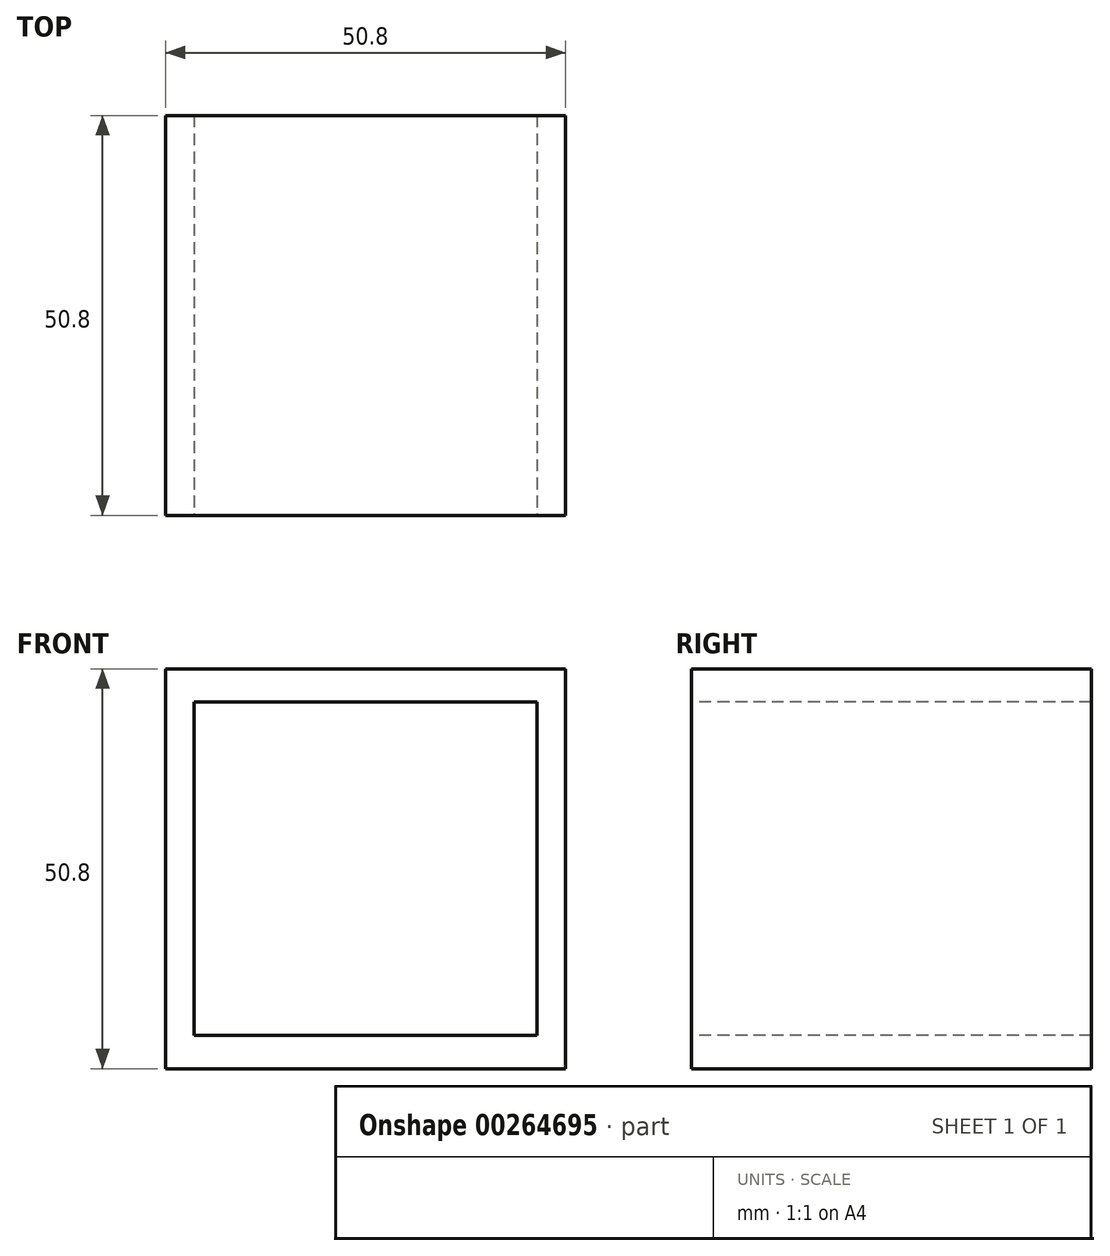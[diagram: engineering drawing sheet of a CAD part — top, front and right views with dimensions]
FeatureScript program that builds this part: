
annotation { "Feature Type Name" : "Feature", "Feature Type Description" : "" }
export const myFeature = defineFeature(function(context is Context, id is Id, definition is map)
    precondition{}
    {
        {
            var Q0;
            Q0=qCreatedBy(makeId("Front.planeOp"),FACE);
            var sketch = newSketch(context, id + "F0", { "sketchPlane" : qUnion([Q0])});
            skLineSegment(sketch, "E0.bottom", {"start": v(-25.4, 25.4) * mm, "end": v(25.4, 25.4) * mm});
            skLineSegment(sketch, "E0.top", {"start": v(-25.4, -25.4) * mm, "end": v(25.4, -25.4) * mm});
            skLineSegment(sketch, "E0.left", {"start": v(-25.4, 25.4) * mm, "end": v(-25.4, -25.4) * mm});
            skLineSegment(sketch, "E0.right", {"start": v(25.4, 25.4) * mm, "end": v(25.4, -25.4) * mm});
            skPoint(sketch, "E0.middle", {"position": v(0, 0) * mm});
            skSolve(sketch);
        }
        {
            var Q0;
            Q0=makeQuery(id+"F0.imprint","IMPRINT",FACE,{"disambiguationData":[TD([[makeQuery(id+"F0.imprint","IMPRINT",EDGE,{"derivedFrom":sQuery(id+"F0.wireOp",EDGE,"E0.bottom")}),-1.0]])]});
            var sketch = newSketch(context, id + "F1", { "sketchPlane" : qUnion([Q0])});
            skLineSegment(sketch, "E1.bottom", {"start": v(21.77, 21.2) * mm, "end": v(-21.77, 21.2) * mm});
            skLineSegment(sketch, "E1.top", {"start": v(21.77, -21.2) * mm, "end": v(-21.77, -21.2) * mm});
            skLineSegment(sketch, "E1.left", {"start": v(21.77, 21.2) * mm, "end": v(21.77, -21.2) * mm});
            skLineSegment(sketch, "E1.right", {"start": v(-21.77, 21.2) * mm, "end": v(-21.77, -21.2) * mm});
            skPoint(sketch, "E1.middle", {"position": v(0, 0) * mm});
            skSolve(sketch);
        }
        {
            var Q0;
            Q0=sQuery(id+"F0.wireOp",EDGE,"E0.bottom");
            var Q1;
            Q1=sQuery(id+"F0.wireOp",EDGE,"E0.right");
            var Q2;
            Q2=sQuery(id+"F0.wireOp",EDGE,"E0.top");
            var Q3;
            Q3=sQuery(id+"F0.wireOp",EDGE,"E0.left");
            var Q4;
            Q4=sQuery(id+"F1.wireOp",EDGE,"E1.bottom");
            var Q5;
            Q5=sQuery(id+"F1.wireOp",EDGE,"E1.left");
            var Q6;
            Q6=sQuery(id+"F1.wireOp",EDGE,"E1.top");
            var Q7;
            Q7=sQuery(id+"F1.wireOp",EDGE,"E1.right");
            extrude(context, id + "F2", {"bodyType" : ToolBodyType.SURFACE, "surfaceEntities" : qUnion([Q0, Q1, Q2, Q3, Q4, Q5, Q6, Q7]), "depth" : 50.8 * mm});
        }
    });
